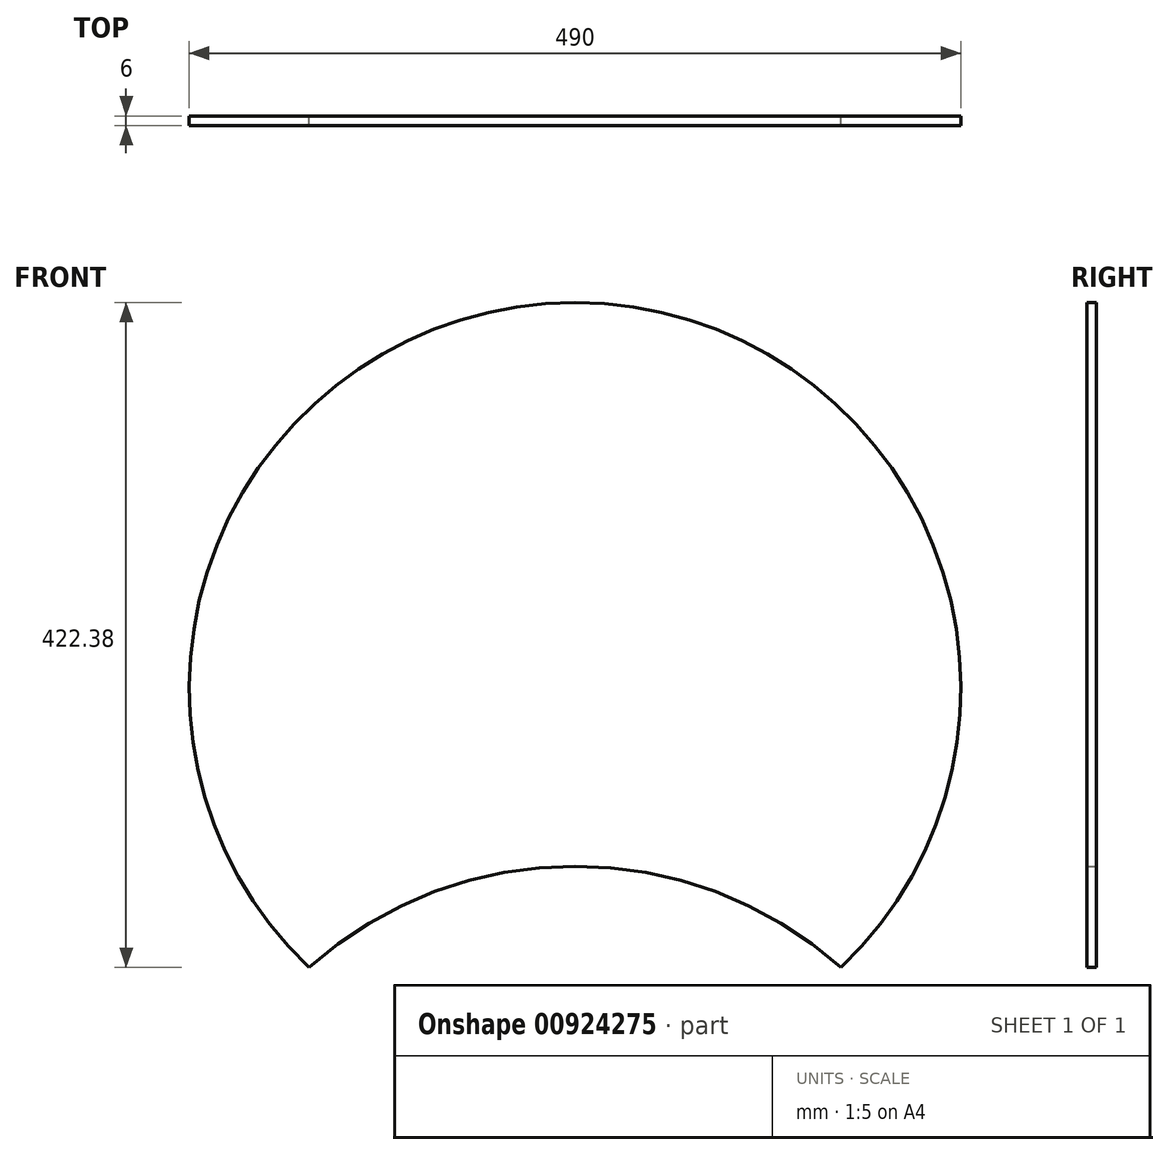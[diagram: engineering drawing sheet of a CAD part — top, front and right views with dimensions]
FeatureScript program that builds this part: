
annotation { "Feature Type Name" : "Feature", "Feature Type Description" : "" }
export const myFeature = defineFeature(function(context is Context, id is Id, definition is map)
    precondition{}
    {
        {
            var Q0;
            Q0=qCreatedBy(makeId("Front.planeOp"),FACE);
            var sketch = newSketch(context, id + "F0", { "sketchPlane" : qUnion([Q0])});
            skCircle(sketch, "E0", {"center": v(0, 0) * mm, "radius": 245 * mm});
            skArc(sketch, "E1", {"start": v(169, -177.38) * mm, "mid": v(0, -113) * mm, "end": v(-169, -177.38) * mm});
            skSolve(sketch);
        }
        {
            var Q0;
            {var subQ0=sQuery(id+"F0.wireOp",EDGE,"E1");Q0=makeQuery(id+"F0.imprint","IMPRINT",FACE,{"disambiguationData":[TD([[makeQuery(id+"F0.imprint","IMPRINT",EDGE,{"derivedFrom":subQ0}),-1.0]])]});}
            extrude(context, id + "F1", {"entities" : qUnion([Q0]), "depth" : 6 * mm, "offsetDistance" : 25.4 * mm});
        }
    });
